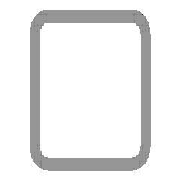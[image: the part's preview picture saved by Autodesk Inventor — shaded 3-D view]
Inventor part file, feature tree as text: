
AUTODESK INVENTOR PART (.ipt)
format: ipt  version: 2025.1 (Build 291241020, 241B)  size: 135,168 bytes
history: native  units: mm (DEFAULTED — no unit token found)
features: other x4, sketch x1, plane x1
ambient origin geometry x8: Origin, YZ Plane, XZ Plane, XY Plane, X Axis, Y Axis, Z Axis, Center Point
bodies: Solid1 (feature_tree), Body (feature_tree)
feature tree (6):
  parser-record x1  (decoder bookkeeping rows leaked as tree rows — omitted from the tree; the rows remain in map.json)
  other  "Driven Length"
  other  "Start Plane"
  other  "End Plane"
  sketch  "Sketch3"  dims[d3=2870.0mm d4=0.0mm d7=4.0mm d9=40.0mm d11=40.0mm d12=2.0mm d13=-0.0mm d14=2870.0mm d15=20.0mm d16=20.0mm d17=90.0deg d18=2870.0mm]
  plane  "Work Plane3"
